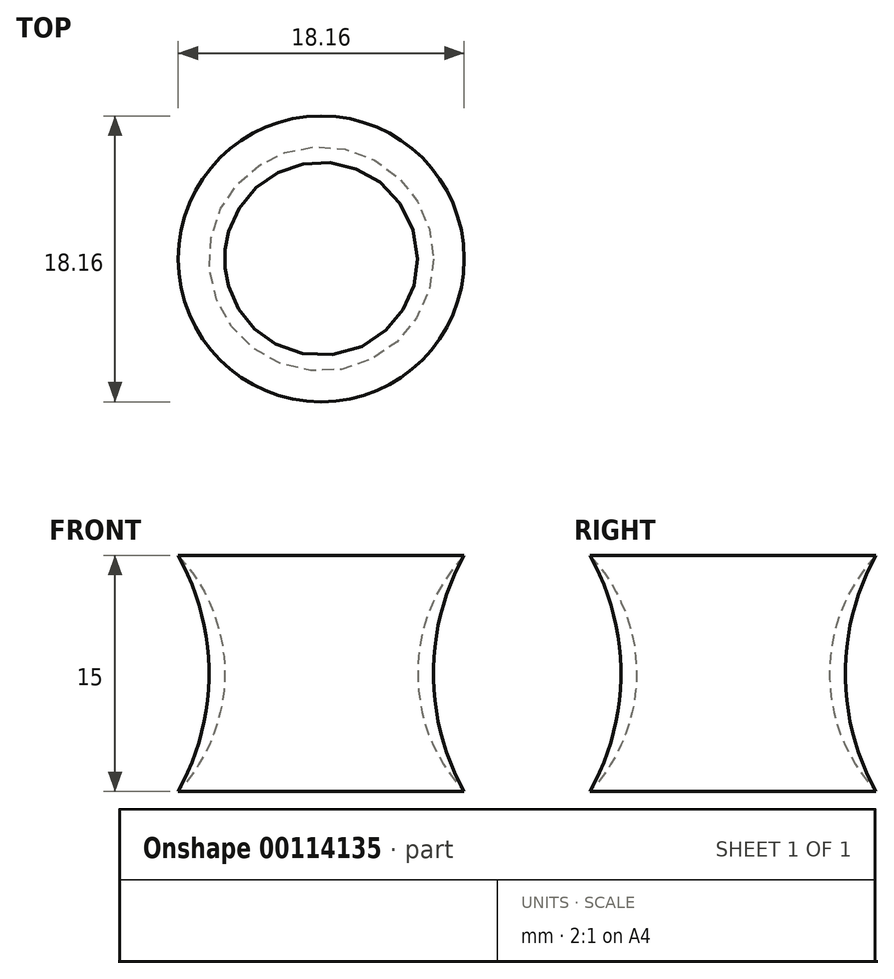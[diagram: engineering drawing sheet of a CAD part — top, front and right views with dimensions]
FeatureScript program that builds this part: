
annotation { "Feature Type Name" : "Feature", "Feature Type Description" : "" }
export const myFeature = defineFeature(function(context is Context, id is Id, definition is map)
    precondition{}
    {
        {
            var Q0;
            Q0=qCreatedBy(makeId("Front.planeOp"),FACE);
            var sketch = newSketch(context, id + "F0", { "sketchPlane" : qUnion([Q0])});
            skArc(sketch, "E0", {"start": v(-9.08, -7.5) * mm, "mid": v(-7.13, 0) * mm, "end": v(-9.08, 7.5) * mm});
            skLineSegment(sketch, "E1", {"start": v(0, 7.5) * mm, "end": v(0, -7.5) * mm});
            skArc(sketch, "E2", {"start": v(-9.08, -7.5) * mm, "mid": v(-6.13, 0) * mm, "end": v(-9.08, 7.5) * mm});
            skLineSegment(sketch, "E3", {"start": v(370.3, 0) * mm, "end": v(0, 0) * mm});
            skLineSegment(sketch, "E4", {"start": v(-6.13, 0) * mm, "end": v(-7.13, 0) * mm});
            skSolve(sketch);
        }
        {
            var Q0;
            Q0=makeQuery(id+"F0.imprint","IMPRINT",FACE,{"disambiguationData":[TD([[makeQuery(id+"F0.imprint","IMPRINT",EDGE,{"derivedFrom":sQuery(id+"F0.wireOp",EDGE,"E0")}),-1.0]])]});
            var Q1;
            Q1=sQuery(id+"F0.wireOp",EDGE,"E1");
            revolve(context, id + "F1", {"entities" : qUnion([Q0]), "axis" : qUnion([Q1]), "revolveType" : RevolveType.FULL});
        }
    });
